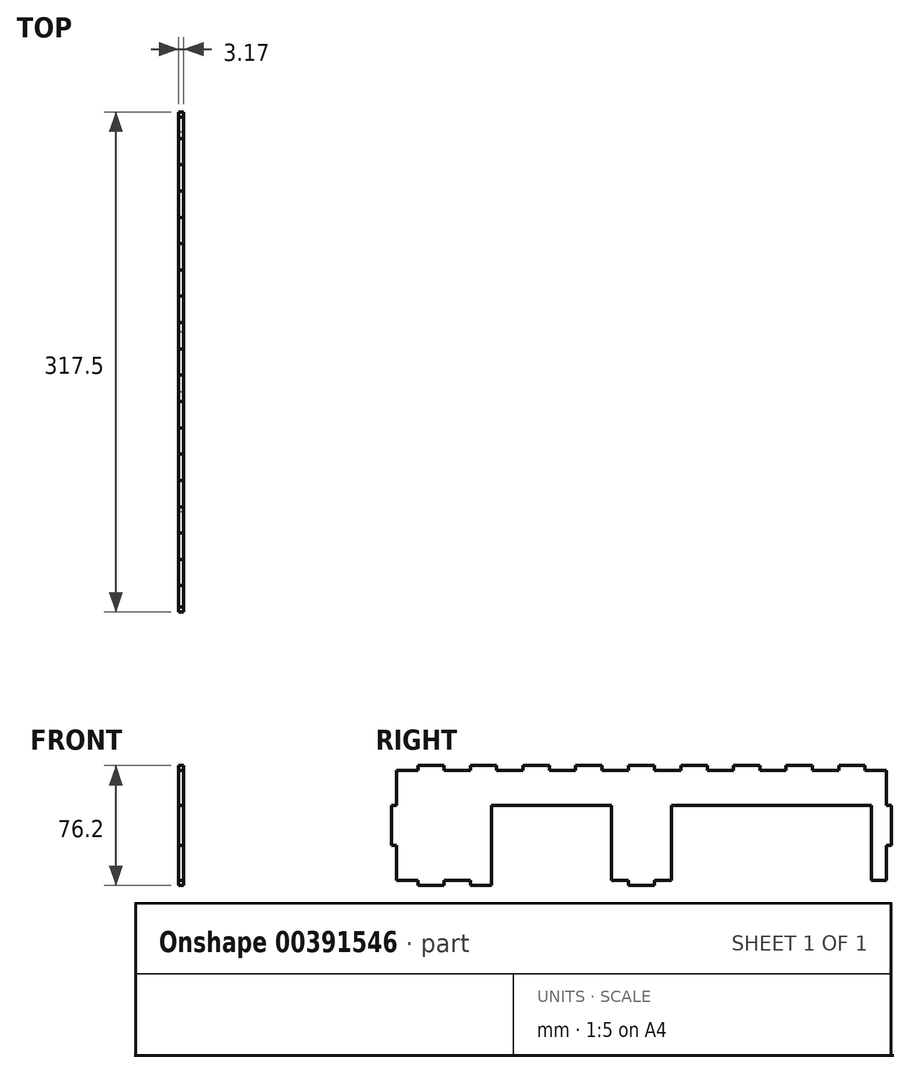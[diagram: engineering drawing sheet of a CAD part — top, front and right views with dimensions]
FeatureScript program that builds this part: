
annotation { "Feature Type Name" : "Feature", "Feature Type Description" : "" }
export const myFeature = defineFeature(function(context is Context, id is Id, definition is map)
    precondition{}
    {
        {
            var Q0;
            Q0=qCreatedBy(makeId("Right.planeOp"),FACE);
            var sketch = newSketch(context, id + "F0", { "sketchPlane" : qUnion([Q0])});
            skLineSegment(sketch, "E0.top", {"start": v(158.75, 38.1) * mm, "end": v(-158.75, 38.1) * mm, "construction": true});
            skLineSegment(sketch, "E0.left", {"start": v(158.75, -38.1) * mm, "end": v(158.75, 38.1) * mm, "construction": true});
            skLineSegment(sketch, "E0.right", {"start": v(-158.75, -38.1) * mm, "end": v(-158.75, 38.1) * mm, "construction": true});
            skPoint(sketch, "E0.middle", {"position": v(0, 0) * mm});
            skLineSegment(sketch, "E1", {"start": v(-155.57, 12.7) * mm, "end": v(-158.75, 12.7) * mm});
            skLineSegment(sketch, "E2", {"start": v(-158.75, 12.7) * mm, "end": v(-158.75, -12.7) * mm});
            skLineSegment(sketch, "E3", {"start": v(-158.75, -12.7) * mm, "end": v(-155.57, -12.7) * mm});
            skLineSegment(sketch, "E4.MirrorCS", {"start": v(155.57, 12.7) * mm, "end": v(158.75, 12.7) * mm});
            skLineSegment(sketch, "E5.MirrorCS", {"start": v(158.75, -12.7) * mm, "end": v(155.57, -12.7) * mm});
            skLineSegment(sketch, "E6.MirrorCS", {"start": v(158.75, 12.7) * mm, "end": v(158.75, -12.7) * mm});
            skLineSegment(sketch, "E7", {"start": v(-142.04, 34.93) * mm, "end": v(-142.04, 38.1) * mm});
            skLineSegment(sketch, "E8", {"start": v(-142.04, 38.1) * mm, "end": v(-125.33, 38.1) * mm});
            skLineSegment(sketch, "E9", {"start": v(-125.33, 38.1) * mm, "end": v(-125.33, 34.93) * mm});
            skLineSegment(sketch, "E10.1.0.0", {"start": v(-125.33, 34.93) * mm, "end": v(-108.62, 34.93) * mm});
            skLineSegment(sketch, "E10.1.0.1", {"start": v(-108.62, 34.93) * mm, "end": v(-108.62, 38.1) * mm});
            skLineSegment(sketch, "E10.1.0.2", {"start": v(-108.62, 38.1) * mm, "end": v(-91.9, 38.1) * mm});
            skLineSegment(sketch, "E10.1.0.3", {"start": v(-91.9, 38.1) * mm, "end": v(-91.9, 34.93) * mm});
            skLineSegment(sketch, "E10.2.0.0", {"start": v(-91.9, 34.93) * mm, "end": v(-75.2, 34.93) * mm});
            skLineSegment(sketch, "E10.2.0.1", {"start": v(-75.2, 34.93) * mm, "end": v(-75.2, 38.1) * mm});
            skLineSegment(sketch, "E10.2.0.2", {"start": v(-75.2, 38.1) * mm, "end": v(-58.49, 38.1) * mm});
            skLineSegment(sketch, "E10.2.0.3", {"start": v(-58.49, 38.1) * mm, "end": v(-58.49, 34.93) * mm});
            skLineSegment(sketch, "E10.3.0.0", {"start": v(-58.49, 34.93) * mm, "end": v(-41.78, 34.93) * mm});
            skLineSegment(sketch, "E10.3.0.1", {"start": v(-41.78, 34.93) * mm, "end": v(-41.78, 38.1) * mm});
            skLineSegment(sketch, "E10.3.0.2", {"start": v(-41.78, 38.1) * mm, "end": v(-25.07, 38.1) * mm});
            skLineSegment(sketch, "E10.3.0.3", {"start": v(-25.07, 38.1) * mm, "end": v(-25.07, 34.93) * mm});
            skLineSegment(sketch, "E10.4.0.0", {"start": v(-25.07, 34.93) * mm, "end": v(-8.36, 34.93) * mm});
            skLineSegment(sketch, "E10.4.0.1", {"start": v(-8.36, 34.93) * mm, "end": v(-8.36, 38.1) * mm});
            skLineSegment(sketch, "E10.4.0.2", {"start": v(-8.36, 38.1) * mm, "end": v(8.36, 38.1) * mm});
            skLineSegment(sketch, "E10.4.0.3", {"start": v(8.36, 38.1) * mm, "end": v(8.36, 34.93) * mm});
            skLineSegment(sketch, "E10.5.0.0", {"start": v(8.36, 34.93) * mm, "end": v(25.07, 34.93) * mm});
            skLineSegment(sketch, "E10.5.0.1", {"start": v(25.07, 34.93) * mm, "end": v(25.07, 38.1) * mm});
            skLineSegment(sketch, "E10.5.0.2", {"start": v(25.07, 38.1) * mm, "end": v(41.78, 38.1) * mm});
            skLineSegment(sketch, "E10.5.0.3", {"start": v(41.78, 38.1) * mm, "end": v(41.78, 34.93) * mm});
            skLineSegment(sketch, "E10.6.0.0", {"start": v(41.78, 34.93) * mm, "end": v(58.49, 34.93) * mm});
            skLineSegment(sketch, "E10.6.0.1", {"start": v(58.49, 34.93) * mm, "end": v(58.49, 38.1) * mm});
            skLineSegment(sketch, "E10.6.0.2", {"start": v(58.49, 38.1) * mm, "end": v(75.2, 38.1) * mm});
            skLineSegment(sketch, "E10.6.0.3", {"start": v(75.2, 38.1) * mm, "end": v(75.2, 34.93) * mm});
            skLineSegment(sketch, "E10.7.0.0", {"start": v(75.2, 34.93) * mm, "end": v(91.9, 34.93) * mm});
            skLineSegment(sketch, "E10.7.0.1", {"start": v(91.9, 34.93) * mm, "end": v(91.9, 38.1) * mm});
            skLineSegment(sketch, "E10.7.0.2", {"start": v(91.9, 38.1) * mm, "end": v(108.62, 38.1) * mm});
            skLineSegment(sketch, "E10.7.0.3", {"start": v(108.62, 38.1) * mm, "end": v(108.62, 34.93) * mm});
            skLineSegment(sketch, "E10.8.0.0", {"start": v(108.62, 34.93) * mm, "end": v(125.33, 34.93) * mm});
            skLineSegment(sketch, "E10.8.0.1", {"start": v(125.33, 34.93) * mm, "end": v(125.33, 38.1) * mm});
            skLineSegment(sketch, "E10.8.0.2", {"start": v(125.33, 38.1) * mm, "end": v(142.04, 38.1) * mm});
            skLineSegment(sketch, "E10.8.0.3", {"start": v(142.04, 38.1) * mm, "end": v(142.04, 34.93) * mm});
            skLineSegment(sketch, "E11.MirrorCS", {"start": v(-108.62, -34.93) * mm, "end": v(-108.62, -38.1) * mm});
            skLineSegment(sketch, "E12.MirrorCS", {"start": v(-142.04, -34.93) * mm, "end": v(-142.04, -38.1) * mm});
            skLineSegment(sketch, "E13.MirrorCS", {"start": v(125.33, -34.93) * mm, "end": v(125.33, -38.1) * mm});
            skLineSegment(sketch, "E14.MirrorCS", {"start": v(-8.36, -34.93) * mm, "end": v(-8.36, -38.1) * mm});
            skLineSegment(sketch, "E15.MirrorCS", {"start": v(108.62, -38.1) * mm, "end": v(108.62, -34.93) * mm});
            skLineSegment(sketch, "E16.MirrorCS", {"start": v(-125.33, -38.1) * mm, "end": v(-125.33, -34.93) * mm});
            skLineSegment(sketch, "E17.MirrorCS", {"start": v(142.04, -38.1) * mm, "end": v(142.04, -34.93) * mm});
            skLineSegment(sketch, "E18.MirrorCS", {"start": v(8.36, -38.1) * mm, "end": v(8.36, -34.93) * mm});
            skLineSegment(sketch, "E19.MirrorCS", {"start": v(-125.33, -34.93) * mm, "end": v(-108.62, -34.93) * mm});
            skLineSegment(sketch, "E20.MirrorCS", {"start": v(125.33, -38.1) * mm, "end": v(142.04, -38.1) * mm});
            skLineSegment(sketch, "E21.MirrorCS", {"start": v(-8.36, -38.1) * mm, "end": v(8.36, -38.1) * mm});
            skLineSegment(sketch, "E22.MirrorCS", {"start": v(-142.04, -38.1) * mm, "end": v(-125.33, -38.1) * mm});
            skLineSegment(sketch, "E23.MirrorCS", {"start": v(108.62, -34.93) * mm, "end": v(125.33, -34.93) * mm});
            skLineSegment(sketch, "E24", {"start": v(155.57, -12.7) * mm, "end": v(155.57, -34.93) * mm});
            skLineSegment(sketch, "E25", {"start": v(142.04, -34.93) * mm, "end": v(155.57, -34.93) * mm});
            skLineSegment(sketch, "E26", {"start": v(142.04, 34.93) * mm, "end": v(155.57, 34.93) * mm});
            skLineSegment(sketch, "E27", {"start": v(155.57, 12.7) * mm, "end": v(155.57, 34.93) * mm});
            skLineSegment(sketch, "E28", {"start": v(-142.04, -34.93) * mm, "end": v(-155.57, -34.93) * mm});
            skLineSegment(sketch, "E29", {"start": v(-155.57, -34.93) * mm, "end": v(-155.57, -12.7) * mm});
            skLineSegment(sketch, "E30", {"start": v(-142.04, 34.93) * mm, "end": v(-155.57, 34.93) * mm});
            skLineSegment(sketch, "E31", {"start": v(-155.57, 34.93) * mm, "end": v(-155.57, 12.7) * mm});
            skLineSegment(sketch, "E32.left", {"start": v(95.25, -38.1) * mm, "end": v(95.25, 12.7) * mm});
            skLineSegment(sketch, "E32.right", {"start": v(-95.25, -38.1) * mm, "end": v(-95.25, 12.7) * mm});
            skPoint(sketch, "E32.middle", {"position": v(0, -12.7) * mm});
            skLineSegment(sketch, "E33", {"start": v(-95.25, 12.7) * mm, "end": v(-19.05, 12.7) * mm});
            skLineSegment(sketch, "E34", {"start": v(19.05, 12.7) * mm, "end": v(95.25, 12.7) * mm});
            skLineSegment(sketch, "E35", {"start": v(-19.05, 12.7) * mm, "end": v(-19.05, -34.93) * mm});
            skLineSegment(sketch, "E36", {"start": v(19.05, 12.7) * mm, "end": v(19.05, -34.93) * mm});
            skLineSegment(sketch, "E37", {"start": v(-108.62, -38.1) * mm, "end": v(-95.25, -38.1) * mm});
            skLineSegment(sketch, "E38", {"start": v(-19.05, -34.93) * mm, "end": v(-8.36, -34.93) * mm});
            skLineSegment(sketch, "E39", {"start": v(8.36, -34.93) * mm, "end": v(19.05, -34.93) * mm});
            skLineSegment(sketch, "E40", {"start": v(95.25, -38.1) * mm, "end": v(108.62, -38.1) * mm});
            skLineSegment(sketch, "E41", {"start": v(146.05, -50.56) * mm, "end": v(146.05, 63.56) * mm, "construction": true});
            skLineSegment(sketch, "E42.bottom", {"start": v(95.25, 12.7) * mm, "end": v(146.05, 12.7) * mm});
            skLineSegment(sketch, "E42.top", {"start": v(95.25, -50.56) * mm, "end": v(146.05, -50.56) * mm});
            skLineSegment(sketch, "E42.left", {"start": v(95.25, 12.7) * mm, "end": v(95.25, -50.56) * mm});
            skLineSegment(sketch, "E42.right", {"start": v(146.05, 12.7) * mm, "end": v(146.05, -50.56) * mm});
            skSolve(sketch);
        }
        {
            var Q0;
            Q0=makeQuery(id+"F0.imprint","IMPRINT",FACE,{"disambiguationData":[TD([[makeQuery(id+"F0.imprint","IMPRINT",EDGE,{"derivedFrom":sQuery(id+"F0.wireOp",EDGE,"E1")}),1.0]])]});
            extrude(context, id + "F1", {"entities" : qUnion([Q0]), "depth" : 3.17 * mm});
        }
    });
